# Revit family: Haworth_ComposeStorage_Pedestal
name_source: partatom
category: Furniture Systems
revit_build: Autodesk Revit 2018 (Build: 20170223_1515(x64)
units: mm (PartAtom-declared; Revit-internal decimal feet)

## family parameters
Always vertical = Yes
Cut with Voids When Loaded = No
OmniClass Number = 23.40.70.14.64.21
OmniClass Title = Systems Furniture
Part Type = Normal
Room Calculation Point = No
Round Connector Dimension = Use Diameter
Shared = No
Work Plane-Based = No

## types (6) — shared parameters
Actual Height = 26 1/4"
Actual Width = 15 1/2"
Assembly Code = E2020200
Back Finish = Haworth _ Wood _ White Oak
Base = Yes
Base Finish = Haworth _ Wood _ White Oak
Base Height = 1"
Base Low = Yes
Cabinet Finish = Haworth _ Wood _ White Oak
Chamfer Legs = No
Classic Pull = No
Crescent Pull = No
Custom Size = No
Depth Adjuster = 1"
Description = Haworth - Compose Storage Pedestal
Drawer Finish = Haworth _ Wood _ White Oak
Drawer Height Bottom = 13"
Drawer Height Box = 5 15/16"
Drawer Height Middle = 12"
Drawer Height Top = 12"
Drawer Width Middle = 17 15/16"
Finished Back = Yes
J Pull = No
Linear Pull = No
Manufacturer = Haworth
Max. Depth = 30"
Min. Depth = 18"
Model = BZM
Patterns Pull = Yes
Plynth Base = No
Pull Finish = Haworth _ Paint _ Metallic Champagne
Revision Number = 3
Shelf 1 = No
Side Panel Base = Yes
Size = Verify Final Dim. w/ Haworth
Spacer Finish = Haworth _ Wood _ White Oak
Spacer Height = 0"
Standard Depths = 18, 24, 30 in.
Standard Widths = 15.5 in.
Sustainability Info = http://media.haworth.com
Top Spacer = No
URL = www.haworth.com
URL - Product = www.haworth.com/products/storage/cabinets-towers/compose
Warranty = http://www.haworth.com

## per-type parameters (varying)
| type | Actual Depth | Box Box File | Depth | File File |
| 15.5w 18d Box Box File | 17" | Yes | 18" | No |
| 15.5w 24d Box Box File | 23" | Yes | 24" | No |
| 15.5w 30d Box Box File | 29" | Yes | 30" | No |
| 15.5w 18d File File | 17" | No | 18" | Yes |
| 15.5w 24d File File | 23" | No | 24" | Yes |
| 15.5w 30d File File | 29" | No | 30" | Yes |

## geometry (parser evidence)
native form markers: Sweep x12
no freeform markers — native parametric forms only
